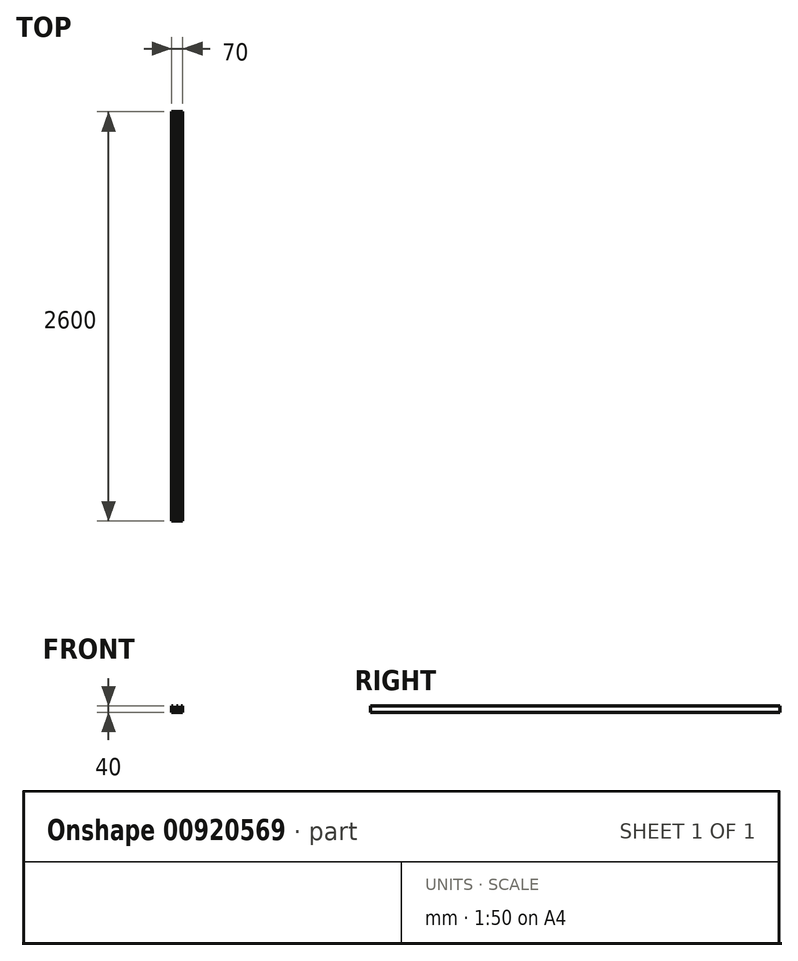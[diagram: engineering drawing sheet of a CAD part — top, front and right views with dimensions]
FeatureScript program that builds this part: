
annotation { "Feature Type Name" : "Feature", "Feature Type Description" : "" }
export const myFeature = defineFeature(function(context is Context, id is Id, definition is map)
    precondition{}
    {
        {
            var Q0;
            Q0=qCreatedBy(makeId("Front.planeOp"),FACE);
            var sketch = newSketch(context, id + "F0", { "sketchPlane" : qUnion([Q0])});
            skLineSegment(sketch, "E0", {"start": v(-35, 25) * mm, "end": v(-35, -15) * mm});
            skLineSegment(sketch, "E1", {"start": v(-35, -15) * mm, "end": v(35, -15) * mm});
            skLineSegment(sketch, "E2", {"start": v(35, -15) * mm, "end": v(35, 25) * mm});
            skLineSegment(sketch, "E3", {"start": v(35, 25) * mm, "end": v(25, 25) * mm});
            skLineSegment(sketch, "E4", {"start": v(25, 25) * mm, "end": v(25, -10) * mm});
            skLineSegment(sketch, "E5", {"start": v(25, -10) * mm, "end": v(5, -10) * mm});
            skLineSegment(sketch, "E6", {"start": v(5, -10) * mm, "end": v(5, 25) * mm});
            skLineSegment(sketch, "E7", {"start": v(5, 25) * mm, "end": v(-5, 25) * mm});
            skLineSegment(sketch, "E8", {"start": v(-5, 25) * mm, "end": v(-5, -10) * mm});
            skLineSegment(sketch, "E9", {"start": v(-5, -10) * mm, "end": v(-25, -10) * mm});
            skLineSegment(sketch, "E10", {"start": v(-25, -10) * mm, "end": v(-25, 25) * mm});
            skLineSegment(sketch, "E11", {"start": v(-25, 25) * mm, "end": v(-35, 25) * mm});
            skSolve(sketch);
        }
        {
            var Q0;
            Q0 = qSketchRegion(id + "F0", true);
            extrude(context, id + "F1", {"entities" : qUnion([Q0]), "depth" : (1930 + 670) * mm, "offsetDistance" : 25 * mm, "symmetric" : true});
        }
    });
